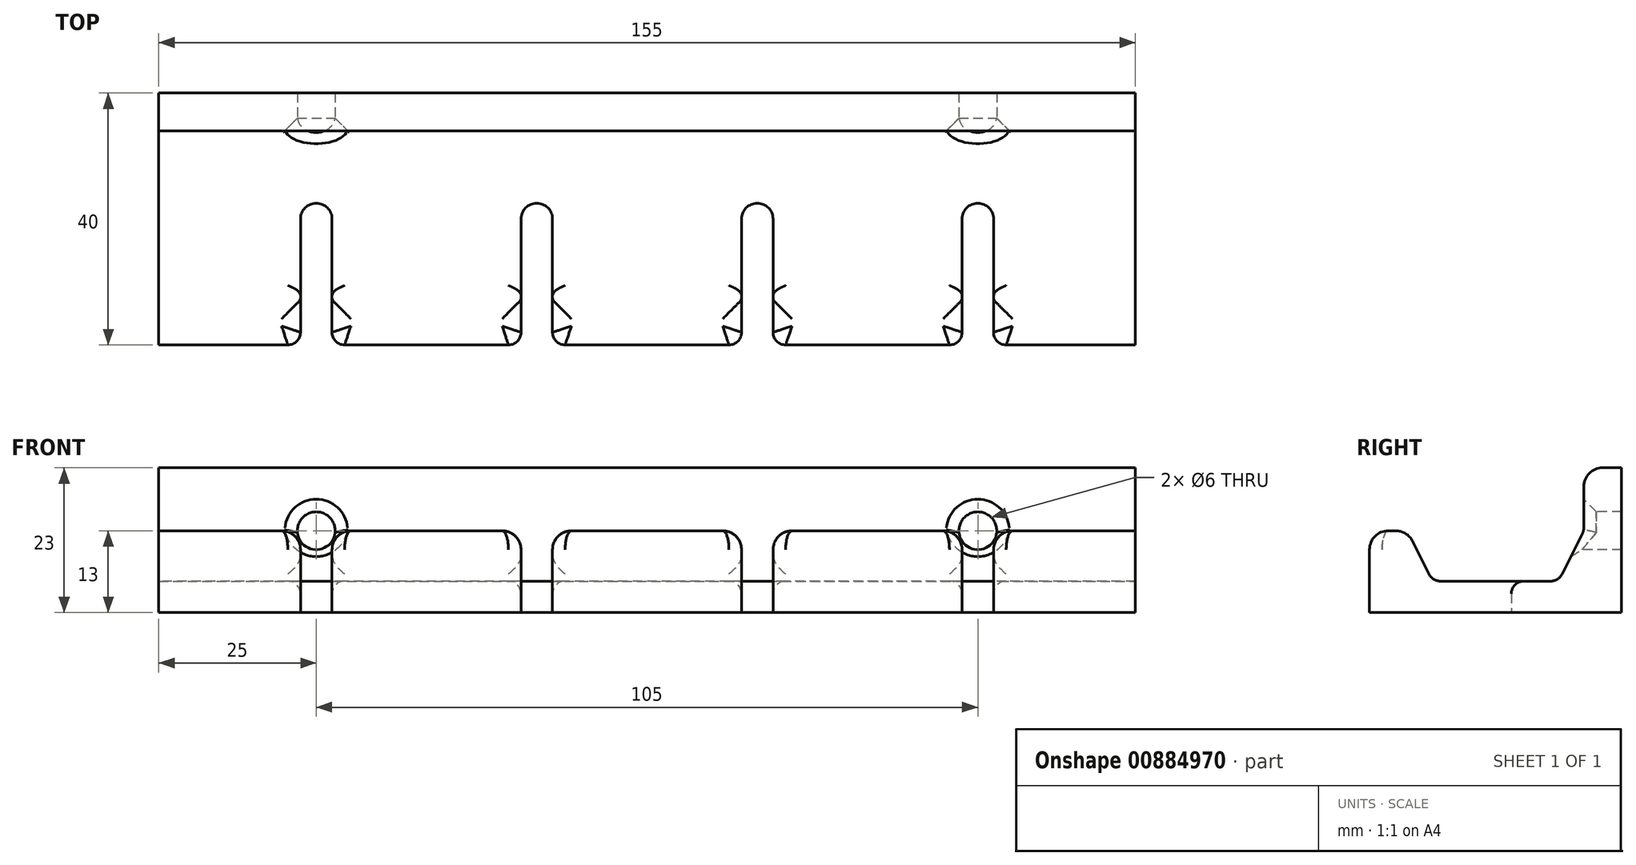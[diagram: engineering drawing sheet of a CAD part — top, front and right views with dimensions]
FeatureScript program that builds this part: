
annotation { "Feature Type Name" : "Feature", "Feature Type Description" : "" }
export const myFeature = defineFeature(function(context is Context, id is Id, definition is map)
    precondition{}
    {
        {
            var Q0;
            Q0=qCreatedBy(makeId("Top.planeOp"),FACE);
            var sketch = newSketch(context, id + "F0", { "sketchPlane" : qUnion([Q0])});
            skLineSegment(sketch, "E0.bottom", {"start": v(-77.5, 20) * mm, "end": v(77.5, 20) * mm});
            skLineSegment(sketch, "E0.top", {"start": v(-77.5, -20) * mm, "end": v(77.5, -20) * mm});
            skLineSegment(sketch, "E0.left", {"start": v(-77.5, 20) * mm, "end": v(-77.5, -20) * mm});
            skLineSegment(sketch, "E0.right", {"start": v(77.5, 20) * mm, "end": v(77.5, -20) * mm});
            skPoint(sketch, "E0.middle", {"position": v(0, 0) * mm});
            skSolve(sketch);
        }
        {
            var Q0;
            Q0=makeQuery(id+"F0.imprint","IMPRINT",FACE,{"disambiguationData":[TD([[makeQuery(id+"F0.imprint","IMPRINT",EDGE,{"derivedFrom":sQuery(id+"F0.wireOp",EDGE,"E0.bottom")}),-1.0]])]});
            extrude(context, id + "F1", {"entities" : qUnion([Q0]), "depth" : 5 * mm, "offsetDistance" : 25 * mm});
        }
        {
            var Q0;
            Q0=makeQuery(id+"F1.opExtrude","CAP_FACE",FACE,{"disambiguationData":[OSD([sQuery(id+"F0.wireOp",EDGE,"E0.bottom"),sQuery(id+"F0.wireOp",EDGE,"E0.top"),sQuery(id+"F0.wireOp",EDGE,"E0.left"),sQuery(id+"F0.wireOp",EDGE,"E0.right")])],"isStart":false});
            var sketch = newSketch(context, id + "F2", { "sketchPlane" : qUnion([Q0])});
            skLineSegment(sketch, "E1.bottom", {"start": v(-77.5, 10) * mm, "end": v(77.5, 10) * mm});
            skLineSegment(sketch, "E1.top", {"start": v(-77.5, -10) * mm, "end": v(77.5, -10) * mm});
            skLineSegment(sketch, "E1.left", {"start": v(-77.5, 10) * mm, "end": v(-77.5, -10) * mm});
            skLineSegment(sketch, "E1.right", {"start": v(77.5, 10) * mm, "end": v(77.5, -10) * mm});
            skPoint(sketch, "E1.middle", {"position": v(0, 0) * mm});
            skLineSegment(sketch, "E2.bottom", {"start": v(-77.5, 20) * mm, "end": v(77.5, 20) * mm});
            skLineSegment(sketch, "E2.top", {"start": v(-77.5, -20) * mm, "end": v(77.5, -20) * mm});
            skLineSegment(sketch, "E2.left", {"start": v(-77.5, 20) * mm, "end": v(-77.5, -20) * mm});
            skLineSegment(sketch, "E2.right", {"start": v(77.5, 20) * mm, "end": v(77.5, -20) * mm});
            skSolve(sketch);
        }
        {
            var Q0;
            {var subQ0=sQuery(id+"F2.wireOp",EDGE,"E1.bottom");Q0=makeQuery(id+"F2.imprint","IMPRINT",FACE,{"disambiguationData":[TD([[makeQuery(id+"F2.imprint","IMPRINT",EDGE,{"derivedFrom":subQ0}),1.0]])]});}
            var Q1;
            {var subQ0=sQuery(id+"F2.wireOp",EDGE,"E1.top");Q1=makeQuery(id+"F2.imprint","IMPRINT",FACE,{"disambiguationData":[TD([[makeQuery(id+"F2.imprint","IMPRINT",EDGE,{"derivedFrom":subQ0}),-1.0]])]});}
            extrude(context, id + "F3", {"entities" : qUnion([Q0, Q1]), "operationType" : NewBodyOperationType.ADD, "depth" : 8 * mm, "offsetDistance" : 25 * mm});
        }
        {
            var Q0;
            Q0=makeQuery(id+"F3.opExtrude","CAP_EDGE",EDGE,{"disambiguationData":[OSD([sQuery(id+"F2.wireOp",EDGE,"E1.bottom")])],"isStart":false});
            chamfer(context, id + "F4", {"entities" : qUnion([Q0]), "chamferType" : ChamferType.TWO_OFFSETS, "width1" : 8 * mm, "oppositeDirection" : true, "width2" : 4 * mm});
        }
        {
            var Q0;
            Q0=makeQuery(id+"F3.opExtrude","CAP_EDGE",EDGE,{"disambiguationData":[OSD([sQuery(id+"F2.wireOp",EDGE,"E1.top")])],"isStart":false});
            chamfer(context, id + "F5", {"entities" : qUnion([Q0]), "chamferType" : ChamferType.TWO_OFFSETS, "width1" : 8 * mm, "oppositeDirection" : false, "width2" : 4 * mm, "tangentPropagation" : true});
        }
        {
            var Q0;
            Q0=makeQuery(id+"F0.imprint","IMPRINT",FACE,{"disambiguationData":[TD([[makeQuery(id+"F0.imprint","IMPRINT",EDGE,{"derivedFrom":sQuery(id+"F0.wireOp",EDGE,"E0.bottom")}),-1.0]])]});
            var sketch = newSketch(context, id + "F6", { "sketchPlane" : qUnion([Q0])});
            skCircle(sketch, "E3", {"center": v(-52.5, 0) * mm, "radius": 2.5 * mm});
            skCircle(sketch, "E4.1.0.0", {"center": v(-17.5, 0) * mm, "radius": 2.5 * mm});
            skCircle(sketch, "E4.2.0.0", {"center": v(17.5, 0) * mm, "radius": 2.5 * mm});
            skCircle(sketch, "E4.3.0.0", {"center": v(52.5, 0) * mm, "radius": 2.5 * mm});
            skLineSegment(sketch, "E4.direction1", {"start": v(-52.5, 0) * mm, "end": v(-17.5, 0) * mm, "construction": true});
            skLineSegment(sketch, "E5", {"start": v(-50, 0) * mm, "end": v(-50, -25) * mm});
            skLineSegment(sketch, "E6", {"start": v(-55, 0) * mm, "end": v(-55, -25) * mm});
            skLineSegment(sketch, "E7", {"start": v(-20, 0) * mm, "end": v(-20, -25) * mm});
            skLineSegment(sketch, "E8", {"start": v(-80.14, 0) * mm, "end": v(82.26, 0) * mm, "construction": true});
            skLineSegment(sketch, "E9", {"start": v(-15, 0) * mm, "end": v(-15, -25) * mm});
            skLineSegment(sketch, "E10", {"start": v(15, 0) * mm, "end": v(15, -25) * mm});
            skLineSegment(sketch, "E11", {"start": v(20, 0) * mm, "end": v(20, -25) * mm});
            skLineSegment(sketch, "E12", {"start": v(50, 0) * mm, "end": v(50, -25) * mm});
            skLineSegment(sketch, "E13", {"start": v(55, 0) * mm, "end": v(55, -25) * mm});
            skLineSegment(sketch, "E14", {"start": v(-50, -25) * mm, "end": v(-55, -25) * mm});
            skLineSegment(sketch, "E15", {"start": v(-20, -25) * mm, "end": v(-15, -25) * mm});
            skLineSegment(sketch, "E16", {"start": v(15, -25) * mm, "end": v(20, -25) * mm});
            skLineSegment(sketch, "E17", {"start": v(50, -25) * mm, "end": v(55, -25) * mm});
            skSolve(sketch);
        }
        {
            var Q0;
            Q0=qSketchRegion(id+"F6",true);
            extrude(context, id + "F7", {"entities" : qUnion([Q0]), "operationType" : NewBodyOperationType.REMOVE, "depth" : 25 * mm, "offsetDistance" : 25 * mm});
        }
        {
            var Q0;
            Q0=makeQuery(id+"F3.opExtrude","CAP_FACE",FACE,{"disambiguationData":[OSD([sQuery(id+"F2.wireOp",EDGE,"E1.bottom"),sQuery(id+"F2.wireOp",EDGE,"E2.bottom"),sQuery(id+"F2.wireOp",EDGE,"E2.left"),sQuery(id+"F2.wireOp",EDGE,"E2.right")])],"isStart":false});
            extrude(context, id + "F8", {"entities" : qUnion([Q0]), "operationType" : NewBodyOperationType.ADD, "depth" : 10 * mm, "offsetDistance" : 25 * mm});
        }
        {
            var Q0;
            Q0=makeQuery(id+"F8.opExtrude","SWEPT_FACE",FACE,{"disambiguationData":[OSD([sQuery(id+"F2.wireOp",EDGE,"E1.bottom"),sQuery(id+"F2.wireOp",EDGE,"E2.bottom"),sQuery(id+"F2.wireOp",EDGE,"E2.left"),sQuery(id+"F2.wireOp",EDGE,"E2.right")])]});
            var sketch = newSketch(context, id + "F9", { "sketchPlane" : qUnion([Q0])});
            skCircle(sketch, "E18", {"center": v(-52.5, 13) * mm, "radius": 3 * mm});
            skCircle(sketch, "E19", {"center": v(52.5, 13) * mm, "radius": 3 * mm});
            skSolve(sketch);
        }
        {
            var Q0;
            Q0=qSketchRegion(id+"F9",true);
            extrude(context, id + "F10", {"entities" : qUnion([Q0]), "operationType" : NewBodyOperationType.REMOVE, "oppositeDirection" : true, "depth" : 15 * mm, "offsetDistance" : 25 * mm, "hasSecondDirection" : true, "secondDirectionOppositeDirection" : false, "secondDirectionDepth" : 15 * mm});
        }
        {
            var Q0;
            Q0=makeQuery(id+"F10.boolean.opBoolean","INTERSECT",EDGE,{"derivedFrom":[makeQuery(id+"F4.opChamfer","BLEND_FACE",FACE,{"disambiguationData":[OSD([sQuery(id+"F2.wireOp",EDGE,"E1.bottom")])]}),makeQuery(id+"F10.opExtrude","SWEPT_FACE",FACE,{"disambiguationData":[OSD([sQuery(id+"F9.wireOp",EDGE,"E18")])]})]});
            var Q1;
            Q1=makeQuery(id+"F10.boolean.opBoolean","INTERSECT",EDGE,{"derivedFrom":[makeQuery(id+"F8.opExtrude","SWEPT_FACE",FACE,{"disambiguationData":[OSD([sQuery(id+"F2.wireOp",EDGE,"E1.bottom"),sQuery(id+"F2.wireOp",EDGE,"E2.bottom"),sQuery(id+"F2.wireOp",EDGE,"E2.left"),sQuery(id+"F2.wireOp",EDGE,"E2.right")])]}),makeQuery(id+"F10.opExtrude","SWEPT_FACE",FACE,{"disambiguationData":[OSD([sQuery(id+"F9.wireOp",EDGE,"E18")])]})]});
            var Q2;
            Q2=makeQuery(id+"F10.boolean.opBoolean","INTERSECT",EDGE,{"derivedFrom":[makeQuery(id+"F4.opChamfer","BLEND_FACE",FACE,{"disambiguationData":[OSD([sQuery(id+"F2.wireOp",EDGE,"E1.bottom")])]}),makeQuery(id+"F10.opExtrude","SWEPT_FACE",FACE,{"disambiguationData":[OSD([sQuery(id+"F9.wireOp",EDGE,"E19")])]})]});
            var Q3;
            Q3=makeQuery(id+"F10.boolean.opBoolean","INTERSECT",EDGE,{"derivedFrom":[makeQuery(id+"F8.opExtrude","SWEPT_FACE",FACE,{"disambiguationData":[OSD([sQuery(id+"F2.wireOp",EDGE,"E1.bottom"),sQuery(id+"F2.wireOp",EDGE,"E2.bottom"),sQuery(id+"F2.wireOp",EDGE,"E2.left"),sQuery(id+"F2.wireOp",EDGE,"E2.right")])]}),makeQuery(id+"F10.opExtrude","SWEPT_FACE",FACE,{"disambiguationData":[OSD([sQuery(id+"F9.wireOp",EDGE,"E19")])]})]});
            chamfer(context, id + "F11", {"entities" : qUnion([Q0, Q1, Q2, Q3]), "width" : 2 * mm, "tangentPropagation" : true});
        }
        {
            var Q0;
            Q0=makeQuery(id+"F7.boolean.opBoolean","INTERSECT",EDGE,{"derivedFrom":[makeQuery(id+"F1.opExtrude","CAP_FACE",FACE,{"disambiguationData":[OSD([sQuery(id+"F0.wireOp",EDGE,"E0.bottom"),sQuery(id+"F0.wireOp",EDGE,"E0.top"),sQuery(id+"F0.wireOp",EDGE,"E0.left"),sQuery(id+"F0.wireOp",EDGE,"E0.right")])],"isStart":false}),makeQuery(id+"F7.opExtrude","SWEPT_FACE",FACE,{"disambiguationData":[OSD([sQuery(id+"F6.wireOp",EDGE,"E6")])]})]});
            var Q1;
            Q1=makeQuery(id+"F7.boolean.opBoolean","INTERSECT",EDGE,{"derivedFrom":[makeQuery(id+"F1.opExtrude","CAP_FACE",FACE,{"disambiguationData":[OSD([sQuery(id+"F0.wireOp",EDGE,"E0.bottom"),sQuery(id+"F0.wireOp",EDGE,"E0.top"),sQuery(id+"F0.wireOp",EDGE,"E0.left"),sQuery(id+"F0.wireOp",EDGE,"E0.right")])],"isStart":false}),makeQuery(id+"F7.opExtrude","SWEPT_FACE",FACE,{"disambiguationData":[OSD([sQuery(id+"F6.wireOp",EDGE,"E3")])]})]});
            var Q2;
            Q2=makeQuery(id+"F7.boolean.opBoolean","INTERSECT",EDGE,{"derivedFrom":[makeQuery(id+"F1.opExtrude","CAP_FACE",FACE,{"disambiguationData":[OSD([sQuery(id+"F0.wireOp",EDGE,"E0.bottom"),sQuery(id+"F0.wireOp",EDGE,"E0.top"),sQuery(id+"F0.wireOp",EDGE,"E0.left"),sQuery(id+"F0.wireOp",EDGE,"E0.right")])],"isStart":false}),makeQuery(id+"F7.opExtrude","SWEPT_FACE",FACE,{"disambiguationData":[OSD([sQuery(id+"F6.wireOp",EDGE,"E5")])]})]});
            var Q3;
            Q3=makeQuery(id+"F7.boolean.opBoolean","INTERSECT",EDGE,{"derivedFrom":[makeQuery(id+"F1.opExtrude","CAP_FACE",FACE,{"disambiguationData":[OSD([sQuery(id+"F0.wireOp",EDGE,"E0.bottom"),sQuery(id+"F0.wireOp",EDGE,"E0.top"),sQuery(id+"F0.wireOp",EDGE,"E0.left"),sQuery(id+"F0.wireOp",EDGE,"E0.right")])],"isStart":false}),makeQuery(id+"F7.opExtrude","SWEPT_FACE",FACE,{"disambiguationData":[OSD([sQuery(id+"F6.wireOp",EDGE,"E7")])]})]});
            var Q4;
            Q4=makeQuery(id+"F7.boolean.opBoolean","INTERSECT",EDGE,{"derivedFrom":[makeQuery(id+"F1.opExtrude","CAP_FACE",FACE,{"disambiguationData":[OSD([sQuery(id+"F0.wireOp",EDGE,"E0.bottom"),sQuery(id+"F0.wireOp",EDGE,"E0.top"),sQuery(id+"F0.wireOp",EDGE,"E0.left"),sQuery(id+"F0.wireOp",EDGE,"E0.right")])],"isStart":false}),makeQuery(id+"F7.opExtrude","SWEPT_FACE",FACE,{"disambiguationData":[OSD([sQuery(id+"F6.wireOp",EDGE,"E4.1.0.0")])]})]});
            var Q5;
            Q5=makeQuery(id+"F7.boolean.opBoolean","INTERSECT",EDGE,{"derivedFrom":[makeQuery(id+"F1.opExtrude","CAP_FACE",FACE,{"disambiguationData":[OSD([sQuery(id+"F0.wireOp",EDGE,"E0.bottom"),sQuery(id+"F0.wireOp",EDGE,"E0.top"),sQuery(id+"F0.wireOp",EDGE,"E0.left"),sQuery(id+"F0.wireOp",EDGE,"E0.right")])],"isStart":false}),makeQuery(id+"F7.opExtrude","SWEPT_FACE",FACE,{"disambiguationData":[OSD([sQuery(id+"F6.wireOp",EDGE,"E9")])]})]});
            var Q6;
            Q6=makeQuery(id+"F7.boolean.opBoolean","INTERSECT",EDGE,{"derivedFrom":[makeQuery(id+"F1.opExtrude","CAP_FACE",FACE,{"disambiguationData":[OSD([sQuery(id+"F0.wireOp",EDGE,"E0.bottom"),sQuery(id+"F0.wireOp",EDGE,"E0.top"),sQuery(id+"F0.wireOp",EDGE,"E0.left"),sQuery(id+"F0.wireOp",EDGE,"E0.right")])],"isStart":false}),makeQuery(id+"F7.opExtrude","SWEPT_FACE",FACE,{"disambiguationData":[OSD([sQuery(id+"F6.wireOp",EDGE,"E10")])]})]});
            var Q7;
            Q7=makeQuery(id+"F7.boolean.opBoolean","INTERSECT",EDGE,{"derivedFrom":[makeQuery(id+"F1.opExtrude","CAP_FACE",FACE,{"disambiguationData":[OSD([sQuery(id+"F0.wireOp",EDGE,"E0.bottom"),sQuery(id+"F0.wireOp",EDGE,"E0.top"),sQuery(id+"F0.wireOp",EDGE,"E0.left"),sQuery(id+"F0.wireOp",EDGE,"E0.right")])],"isStart":false}),makeQuery(id+"F7.opExtrude","SWEPT_FACE",FACE,{"disambiguationData":[OSD([sQuery(id+"F6.wireOp",EDGE,"E12")])]})]});
            var Q8;
            Q8=makeQuery(id+"F7.boolean.opBoolean","COPY",EDGE,{"derivedFrom":makeQuery(id+"F7.opExtrude","CAP_EDGE",EDGE,{"disambiguationData":[OSD([sQuery(id+"F6.wireOp",EDGE,"E5")])],"isStart":true})});
            var Q9;
            Q9=makeQuery(id+"F7.boolean.opBoolean","COPY",EDGE,{"derivedFrom":makeQuery(id+"F7.opExtrude","CAP_EDGE",EDGE,{"disambiguationData":[OSD([sQuery(id+"F6.wireOp",EDGE,"E9")])],"isStart":true})});
            var Q10;
            Q10=makeQuery(id+"F7.boolean.opBoolean","COPY",EDGE,{"derivedFrom":makeQuery(id+"F7.opExtrude","CAP_EDGE",EDGE,{"disambiguationData":[OSD([sQuery(id+"F6.wireOp",EDGE,"E11")])],"isStart":true})});
            var Q11;
            Q11=makeQuery(id+"F7.boolean.opBoolean","COPY",EDGE,{"derivedFrom":makeQuery(id+"F7.opExtrude","CAP_EDGE",EDGE,{"disambiguationData":[OSD([sQuery(id+"F6.wireOp",EDGE,"E13")])],"isStart":true})});
            var Q12;
            Q12=makeQuery(id+"F7.boolean.opBoolean","INTERSECT",EDGE,{"derivedFrom":[makeQuery(id+"F3.boolean.opBoolean","MERGE",FACE,{"derivedFrom":[makeQuery(id+"F1.opExtrude","SWEPT_FACE",FACE,{"disambiguationData":[OSD([sQuery(id+"F0.wireOp",EDGE,"E0.top")])]}),makeQuery(id+"F3.opExtrude","SWEPT_FACE",FACE,{"disambiguationData":[OSD([sQuery(id+"F2.wireOp",EDGE,"E2.top")])]})]}),makeQuery(id+"F7.opExtrude","SWEPT_FACE",FACE,{"disambiguationData":[OSD([sQuery(id+"F6.wireOp",EDGE,"E6")])]})]});
            var Q13;
            Q13=makeQuery(id+"F7.boolean.opBoolean","INTERSECT",EDGE,{"derivedFrom":[makeQuery(id+"F3.boolean.opBoolean","MERGE",FACE,{"derivedFrom":[makeQuery(id+"F1.opExtrude","SWEPT_FACE",FACE,{"disambiguationData":[OSD([sQuery(id+"F0.wireOp",EDGE,"E0.top")])]}),makeQuery(id+"F3.opExtrude","SWEPT_FACE",FACE,{"disambiguationData":[OSD([sQuery(id+"F2.wireOp",EDGE,"E2.top")])]})]}),makeQuery(id+"F7.opExtrude","SWEPT_FACE",FACE,{"disambiguationData":[OSD([sQuery(id+"F6.wireOp",EDGE,"E5")])]})]});
            var Q14;
            Q14=makeQuery(id+"F7.boolean.opBoolean","INTERSECT",EDGE,{"derivedFrom":[makeQuery(id+"F3.boolean.opBoolean","MERGE",FACE,{"derivedFrom":[makeQuery(id+"F1.opExtrude","SWEPT_FACE",FACE,{"disambiguationData":[OSD([sQuery(id+"F0.wireOp",EDGE,"E0.top")])]}),makeQuery(id+"F3.opExtrude","SWEPT_FACE",FACE,{"disambiguationData":[OSD([sQuery(id+"F2.wireOp",EDGE,"E2.top")])]})]}),makeQuery(id+"F7.opExtrude","SWEPT_FACE",FACE,{"disambiguationData":[OSD([sQuery(id+"F6.wireOp",EDGE,"E7")])]})]});
            var Q15;
            Q15=makeQuery(id+"F7.boolean.opBoolean","INTERSECT",EDGE,{"derivedFrom":[makeQuery(id+"F3.boolean.opBoolean","MERGE",FACE,{"derivedFrom":[makeQuery(id+"F1.opExtrude","SWEPT_FACE",FACE,{"disambiguationData":[OSD([sQuery(id+"F0.wireOp",EDGE,"E0.top")])]}),makeQuery(id+"F3.opExtrude","SWEPT_FACE",FACE,{"disambiguationData":[OSD([sQuery(id+"F2.wireOp",EDGE,"E2.top")])]})]}),makeQuery(id+"F7.opExtrude","SWEPT_FACE",FACE,{"disambiguationData":[OSD([sQuery(id+"F6.wireOp",EDGE,"E9")])]})]});
            var Q16;
            Q16=makeQuery(id+"F7.boolean.opBoolean","INTERSECT",EDGE,{"derivedFrom":[makeQuery(id+"F3.boolean.opBoolean","MERGE",FACE,{"derivedFrom":[makeQuery(id+"F1.opExtrude","SWEPT_FACE",FACE,{"disambiguationData":[OSD([sQuery(id+"F0.wireOp",EDGE,"E0.top")])]}),makeQuery(id+"F3.opExtrude","SWEPT_FACE",FACE,{"disambiguationData":[OSD([sQuery(id+"F2.wireOp",EDGE,"E2.top")])]})]}),makeQuery(id+"F7.opExtrude","SWEPT_FACE",FACE,{"disambiguationData":[OSD([sQuery(id+"F6.wireOp",EDGE,"E10")])]})]});
            var Q17;
            Q17=makeQuery(id+"F7.boolean.opBoolean","INTERSECT",EDGE,{"derivedFrom":[makeQuery(id+"F3.boolean.opBoolean","MERGE",FACE,{"derivedFrom":[makeQuery(id+"F1.opExtrude","SWEPT_FACE",FACE,{"disambiguationData":[OSD([sQuery(id+"F0.wireOp",EDGE,"E0.top")])]}),makeQuery(id+"F3.opExtrude","SWEPT_FACE",FACE,{"disambiguationData":[OSD([sQuery(id+"F2.wireOp",EDGE,"E2.top")])]})]}),makeQuery(id+"F7.opExtrude","SWEPT_FACE",FACE,{"disambiguationData":[OSD([sQuery(id+"F6.wireOp",EDGE,"E11")])]})]});
            var Q18;
            Q18=makeQuery(id+"F7.boolean.opBoolean","INTERSECT",EDGE,{"derivedFrom":[makeQuery(id+"F3.boolean.opBoolean","MERGE",FACE,{"derivedFrom":[makeQuery(id+"F1.opExtrude","SWEPT_FACE",FACE,{"disambiguationData":[OSD([sQuery(id+"F0.wireOp",EDGE,"E0.top")])]}),makeQuery(id+"F3.opExtrude","SWEPT_FACE",FACE,{"disambiguationData":[OSD([sQuery(id+"F2.wireOp",EDGE,"E2.top")])]})]}),makeQuery(id+"F7.opExtrude","SWEPT_FACE",FACE,{"disambiguationData":[OSD([sQuery(id+"F6.wireOp",EDGE,"E12")])]})]});
            var Q19;
            Q19=makeQuery(id+"F7.boolean.opBoolean","INTERSECT",EDGE,{"derivedFrom":[makeQuery(id+"F3.boolean.opBoolean","MERGE",FACE,{"derivedFrom":[makeQuery(id+"F1.opExtrude","SWEPT_FACE",FACE,{"disambiguationData":[OSD([sQuery(id+"F0.wireOp",EDGE,"E0.top")])]}),makeQuery(id+"F3.opExtrude","SWEPT_FACE",FACE,{"disambiguationData":[OSD([sQuery(id+"F2.wireOp",EDGE,"E2.top")])]})]}),makeQuery(id+"F7.opExtrude","SWEPT_FACE",FACE,{"disambiguationData":[OSD([sQuery(id+"F6.wireOp",EDGE,"E13")])]})]});
            var Q20;
            {var subQ0=makeQuery(id+"F1.opExtrude","CAP_FACE",FACE,{"disambiguationData":[OSD([sQuery(id+"F0.wireOp",EDGE,"E0.bottom"),sQuery(id+"F0.wireOp",EDGE,"E0.top"),sQuery(id+"F0.wireOp",EDGE,"E0.left"),sQuery(id+"F0.wireOp",EDGE,"E0.right")])],"isStart":false});var subQ1=sQuery(id+"F2.wireOp",EDGE,"E1.top");Q20=makeQuery(id+"F7.boolean.opBoolean","SPLIT",EDGE,{"disambiguationData":[TD([makeQuery(id+"F7.opExtrude","SWEPT_FACE",FACE,{"disambiguationData":[OSD([sQuery(id+"F6.wireOp",EDGE,"E9")])]})])],"derivedFrom":makeQuery(id+"F5.opChamfer","BLEND_EDGE",EDGE,{"blendedFrom":[makeQuery(id+"F3.opExtrude","CAP_EDGE",EDGE,{"disambiguationData":[OSD([subQ1])],"isStart":false}),subQ0],"blendedInto":[subQ0]})});}
            var Q21;
            {var subQ0=makeQuery(id+"F1.opExtrude","CAP_FACE",FACE,{"disambiguationData":[OSD([sQuery(id+"F0.wireOp",EDGE,"E0.bottom"),sQuery(id+"F0.wireOp",EDGE,"E0.top"),sQuery(id+"F0.wireOp",EDGE,"E0.left"),sQuery(id+"F0.wireOp",EDGE,"E0.right")])],"isStart":false});var subQ1=sQuery(id+"F2.wireOp",EDGE,"E1.top");Q21=makeQuery(id+"F7.boolean.opBoolean","SPLIT",EDGE,{"disambiguationData":[TD([makeQuery(id+"F7.opExtrude","SWEPT_FACE",FACE,{"disambiguationData":[OSD([sQuery(id+"F6.wireOp",EDGE,"E5")])]})])],"derivedFrom":makeQuery(id+"F5.opChamfer","BLEND_EDGE",EDGE,{"blendedFrom":[makeQuery(id+"F3.opExtrude","CAP_EDGE",EDGE,{"disambiguationData":[OSD([subQ1])],"isStart":false}),subQ0],"blendedInto":[subQ0]})});}
            var Q22;
            {var subQ1=sQuery(id+"F0.wireOp",EDGE,"E0.left");var subQ2=sQuery(id+"F2.wireOp",EDGE,"E1.top");var subQ3=makeQuery(id+"F1.opExtrude","CAP_FACE",FACE,{"disambiguationData":[OSD([sQuery(id+"F0.wireOp",EDGE,"E0.bottom"),sQuery(id+"F0.wireOp",EDGE,"E0.top"),subQ1,sQuery(id+"F0.wireOp",EDGE,"E0.right")])],"isStart":false});Q22=makeQuery(id+"F7.boolean.opBoolean","SPLIT",EDGE,{"disambiguationData":[TD([makeQuery(id+"F1.opExtrude","SWEPT_FACE",FACE,{"disambiguationData":[OSD([subQ1])]})])],"derivedFrom":makeQuery(id+"F5.opChamfer","BLEND_EDGE",EDGE,{"blendedFrom":[makeQuery(id+"F3.opExtrude","CAP_EDGE",EDGE,{"disambiguationData":[OSD([subQ2])],"isStart":false}),subQ3],"blendedInto":[subQ3]})});}
            var Q23;
            {var subQ0=makeQuery(id+"F1.opExtrude","CAP_FACE",FACE,{"disambiguationData":[OSD([sQuery(id+"F0.wireOp",EDGE,"E0.bottom"),sQuery(id+"F0.wireOp",EDGE,"E0.top"),sQuery(id+"F0.wireOp",EDGE,"E0.left"),sQuery(id+"F0.wireOp",EDGE,"E0.right")])],"isStart":false});var subQ1=sQuery(id+"F2.wireOp",EDGE,"E1.top");Q23=makeQuery(id+"F7.boolean.opBoolean","SPLIT",EDGE,{"disambiguationData":[TD([makeQuery(id+"F7.opExtrude","SWEPT_FACE",FACE,{"disambiguationData":[OSD([sQuery(id+"F6.wireOp",EDGE,"E11")])]})])],"derivedFrom":makeQuery(id+"F5.opChamfer","BLEND_EDGE",EDGE,{"blendedFrom":[makeQuery(id+"F3.opExtrude","CAP_EDGE",EDGE,{"disambiguationData":[OSD([subQ1])],"isStart":false}),subQ0],"blendedInto":[subQ0]})});}
            var Q24;
            {var subQ1=sQuery(id+"F2.wireOp",EDGE,"E1.top");var subQ2=sQuery(id+"F0.wireOp",EDGE,"E0.right");var subQ3=makeQuery(id+"F1.opExtrude","CAP_FACE",FACE,{"disambiguationData":[OSD([sQuery(id+"F0.wireOp",EDGE,"E0.bottom"),sQuery(id+"F0.wireOp",EDGE,"E0.top"),sQuery(id+"F0.wireOp",EDGE,"E0.left"),subQ2])],"isStart":false});Q24=makeQuery(id+"F7.boolean.opBoolean","SPLIT",EDGE,{"disambiguationData":[TD([makeQuery(id+"F1.opExtrude","SWEPT_FACE",FACE,{"disambiguationData":[OSD([subQ2])]})])],"derivedFrom":makeQuery(id+"F5.opChamfer","BLEND_EDGE",EDGE,{"blendedFrom":[makeQuery(id+"F3.opExtrude","CAP_EDGE",EDGE,{"disambiguationData":[OSD([subQ1])],"isStart":false}),subQ3],"blendedInto":[subQ3]})});}
            var Q25;
            Q25=makeQuery(id+"F4.opChamfer","BLEND_EDGE",EDGE,{"blendedFrom":[makeQuery(id+"F3.opExtrude","CAP_EDGE",EDGE,{"disambiguationData":[OSD([sQuery(id+"F2.wireOp",EDGE,"E1.bottom")])],"isStart":false}),makeQuery(id+"F1.opExtrude","CAP_FACE",FACE,{"disambiguationData":[OSD([sQuery(id+"F0.wireOp",EDGE,"E0.bottom"),sQuery(id+"F0.wireOp",EDGE,"E0.top"),sQuery(id+"F0.wireOp",EDGE,"E0.left"),sQuery(id+"F0.wireOp",EDGE,"E0.right")])],"isStart":false})],"blendedInto":[makeQuery(id+"F1.opExtrude","CAP_FACE",FACE,{"disambiguationData":[OSD([sQuery(id+"F0.wireOp",EDGE,"E0.bottom"),sQuery(id+"F0.wireOp",EDGE,"E0.top"),sQuery(id+"F0.wireOp",EDGE,"E0.left"),sQuery(id+"F0.wireOp",EDGE,"E0.right")])],"isStart":false})]});
            var Q26;
            {var subQ0=sQuery(id+"F2.wireOp",EDGE,"E1.bottom");var subQ1=sQuery(id+"F2.wireOp",EDGE,"E2.left");var subQ2=sQuery(id+"F2.wireOp",EDGE,"E2.bottom");var subQ3=sQuery(id+"F2.wireOp",EDGE,"E2.right");Q26=makeQuery(id+"F10.boolean.opBoolean","SPLIT",EDGE,{"disambiguationData":[TD([makeQuery(id+"F1.opExtrude","SWEPT_FACE",FACE,{"disambiguationData":[OSD([sQuery(id+"F0.wireOp",EDGE,"E0.left")])]}),makeQuery(id+"F3.opExtrude","SWEPT_FACE",FACE,{"disambiguationData":[OSD([subQ1]),TDD([makeQuery(id+"F2.imprint","IMPRINT",EDGE,{"disambiguationData":[TD([[makeQuery(id+"F2.imprint","INTERSECT",VERTEX,{"derivedFrom":[subQ2,subQ1]}),-1.0]])],"derivedFrom":subQ1})])]}),makeQuery(id+"F3.opExtrude","SWEPT_FACE",FACE,{"disambiguationData":[OSD([subQ1]),TDD([makeQuery(id+"F2.imprint","IMPRINT",EDGE,{"disambiguationData":[TD([[makeQuery(id+"F2.imprint","INTERSECT",VERTEX,{"derivedFrom":[sQuery(id+"F2.wireOp",EDGE,"E2.top"),subQ1]}),1.0]])],"derivedFrom":subQ1})])]}),makeQuery(id+"F4.opChamfer","BLEND_FACE",FACE,{"disambiguationData":[OSD([subQ0])]}),makeQuery(id+"F8.opExtrude","SWEPT_FACE",FACE,{"disambiguationData":[OSD([subQ0,subQ2,subQ1,subQ3])]}),makeQuery(id+"F8.opExtrude","SWEPT_FACE",FACE,{"disambiguationData":[OSD([subQ1])]}),makeQuery(id+"F10.opExtrude","SWEPT_FACE",FACE,{"disambiguationData":[OSD([sQuery(id+"F9.wireOp",EDGE,"E18")])]})])],"derivedFrom":makeQuery(id+"F8.boolean.opBoolean","MERGE",EDGE,{"derivedFrom":[makeQuery(id+"F4.opChamfer","BLEND_EDGE",EDGE,{"blendedFrom":[makeQuery(id+"F3.opExtrude","CAP_EDGE",EDGE,{"disambiguationData":[OSD([subQ0])],"isStart":false}),makeQuery(id+"F3.opExtrude","CAP_FACE",FACE,{"disambiguationData":[OSD([subQ0,subQ2,subQ1,subQ3])],"isStart":false})],"blendedInto":[makeQuery(id+"F3.opExtrude","CAP_FACE",FACE,{"disambiguationData":[OSD([subQ0,subQ2,subQ1,subQ3])],"isStart":false})]}),makeQuery(id+"F8.opExtrude","CAP_EDGE",EDGE,{"disambiguationData":[OSD([subQ0,subQ2,subQ1,subQ3])],"isStart":true})]})});}
            var Q27;
            {var subQ0=sQuery(id+"F2.wireOp",EDGE,"E1.bottom");var subQ1=sQuery(id+"F2.wireOp",EDGE,"E2.right");var subQ2=sQuery(id+"F2.wireOp",EDGE,"E2.left");var subQ3=sQuery(id+"F2.wireOp",EDGE,"E2.bottom");Q27=makeQuery(id+"F10.boolean.opBoolean","SPLIT",EDGE,{"disambiguationData":[TD([makeQuery(id+"F4.opChamfer","BLEND_FACE",FACE,{"disambiguationData":[OSD([subQ0])]}),makeQuery(id+"F8.opExtrude","SWEPT_FACE",FACE,{"disambiguationData":[OSD([subQ0,subQ3,subQ2,subQ1])]}),makeQuery(id+"F10.opExtrude","SWEPT_FACE",FACE,{"disambiguationData":[OSD([sQuery(id+"F9.wireOp",EDGE,"E18")])]}),makeQuery(id+"F10.opExtrude","SWEPT_FACE",FACE,{"disambiguationData":[OSD([sQuery(id+"F9.wireOp",EDGE,"E19")])]})])],"derivedFrom":makeQuery(id+"F8.boolean.opBoolean","MERGE",EDGE,{"derivedFrom":[makeQuery(id+"F4.opChamfer","BLEND_EDGE",EDGE,{"blendedFrom":[makeQuery(id+"F3.opExtrude","CAP_EDGE",EDGE,{"disambiguationData":[OSD([subQ0])],"isStart":false}),makeQuery(id+"F3.opExtrude","CAP_FACE",FACE,{"disambiguationData":[OSD([subQ0,subQ3,subQ2,subQ1])],"isStart":false})],"blendedInto":[makeQuery(id+"F3.opExtrude","CAP_FACE",FACE,{"disambiguationData":[OSD([subQ0,subQ3,subQ2,subQ1])],"isStart":false})]}),makeQuery(id+"F8.opExtrude","CAP_EDGE",EDGE,{"disambiguationData":[OSD([subQ0,subQ3,subQ2,subQ1])],"isStart":true})]})});}
            var Q28;
            {var subQ0=sQuery(id+"F2.wireOp",EDGE,"E2.right");var subQ1=sQuery(id+"F2.wireOp",EDGE,"E2.bottom");var subQ2=sQuery(id+"F2.wireOp",EDGE,"E1.bottom");var subQ3=sQuery(id+"F2.wireOp",EDGE,"E2.left");Q28=makeQuery(id+"F10.boolean.opBoolean","SPLIT",EDGE,{"disambiguationData":[TD([makeQuery(id+"F1.opExtrude","SWEPT_FACE",FACE,{"disambiguationData":[OSD([sQuery(id+"F0.wireOp",EDGE,"E0.right")])]}),makeQuery(id+"F3.opExtrude","SWEPT_FACE",FACE,{"disambiguationData":[OSD([subQ0]),TDD([makeQuery(id+"F2.imprint","IMPRINT",EDGE,{"disambiguationData":[TD([[makeQuery(id+"F2.imprint","INTERSECT",VERTEX,{"derivedFrom":[subQ1,subQ0]}),-1.0]])],"derivedFrom":subQ0})])]}),makeQuery(id+"F3.opExtrude","SWEPT_FACE",FACE,{"disambiguationData":[OSD([subQ0]),TDD([makeQuery(id+"F2.imprint","IMPRINT",EDGE,{"disambiguationData":[TD([[makeQuery(id+"F2.imprint","INTERSECT",VERTEX,{"derivedFrom":[sQuery(id+"F2.wireOp",EDGE,"E2.top"),subQ0]}),1.0]])],"derivedFrom":subQ0})])]}),makeQuery(id+"F4.opChamfer","BLEND_FACE",FACE,{"disambiguationData":[OSD([subQ2])]}),makeQuery(id+"F8.opExtrude","SWEPT_FACE",FACE,{"disambiguationData":[OSD([subQ2,subQ1,subQ3,subQ0])]}),makeQuery(id+"F8.opExtrude","SWEPT_FACE",FACE,{"disambiguationData":[OSD([subQ0])]}),makeQuery(id+"F10.opExtrude","SWEPT_FACE",FACE,{"disambiguationData":[OSD([sQuery(id+"F9.wireOp",EDGE,"E19")])]})])],"derivedFrom":makeQuery(id+"F8.boolean.opBoolean","MERGE",EDGE,{"derivedFrom":[makeQuery(id+"F4.opChamfer","BLEND_EDGE",EDGE,{"blendedFrom":[makeQuery(id+"F3.opExtrude","CAP_EDGE",EDGE,{"disambiguationData":[OSD([subQ2])],"isStart":false}),makeQuery(id+"F3.opExtrude","CAP_FACE",FACE,{"disambiguationData":[OSD([subQ2,subQ1,subQ3,subQ0])],"isStart":false})],"blendedInto":[makeQuery(id+"F3.opExtrude","CAP_FACE",FACE,{"disambiguationData":[OSD([subQ2,subQ1,subQ3,subQ0])],"isStart":false})]}),makeQuery(id+"F8.opExtrude","CAP_EDGE",EDGE,{"disambiguationData":[OSD([subQ2,subQ1,subQ3,subQ0])],"isStart":true})]})});}
            fillet(context, id + "F12", {"entities" : qUnion([Q0, Q1, Q2, Q3, Q4, Q5, Q6, Q7, Q8, Q9, Q10, Q11, Q12, Q13, Q14, Q15, Q16, Q17, Q18, Q19, Q20, Q21, Q22, Q23, Q24, Q25, Q26, Q27, Q28]), "radius" : 2 * mm, "tangentPropagation" : true, "allowEdgeOverflow" : false});
        }
        {
            var Q0;
            Q0=makeQuery(id+"F8.opExtrude","CAP_EDGE",EDGE,{"disambiguationData":[OSD([sQuery(id+"F2.wireOp",EDGE,"E1.bottom"),sQuery(id+"F2.wireOp",EDGE,"E2.bottom"),sQuery(id+"F2.wireOp",EDGE,"E2.left"),sQuery(id+"F2.wireOp",EDGE,"E2.right")])],"isStart":false});
            var Q1;
            {var subQ0=sQuery(id+"F2.wireOp",EDGE,"E2.left");var subQ1=sQuery(id+"F2.wireOp",EDGE,"E2.top");var subQ2=sQuery(id+"F2.wireOp",EDGE,"E1.top");var subQ3=makeQuery(id+"F3.opExtrude","CAP_FACE",FACE,{"disambiguationData":[OSD([subQ2,subQ1,subQ0,sQuery(id+"F2.wireOp",EDGE,"E2.right")])],"isStart":false});Q1=makeQuery(id+"F7.boolean.opBoolean","SPLIT",EDGE,{"disambiguationData":[TD([makeQuery(id+"F1.opExtrude","SWEPT_FACE",FACE,{"disambiguationData":[OSD([sQuery(id+"F0.wireOp",EDGE,"E0.left")])]})])],"derivedFrom":makeQuery(id+"F5.opChamfer","BLEND_EDGE",EDGE,{"blendedFrom":[makeQuery(id+"F3.opExtrude","CAP_EDGE",EDGE,{"disambiguationData":[OSD([subQ2])],"isStart":false}),subQ3],"blendedInto":[subQ3]})});}
            var Q2;
            {var subQ0=sQuery(id+"F2.wireOp",EDGE,"E2.top");Q2=makeQuery(id+"F7.boolean.opBoolean","SPLIT",EDGE,{"disambiguationData":[TD([makeQuery(id+"F1.opExtrude","SWEPT_FACE",FACE,{"disambiguationData":[OSD([sQuery(id+"F0.wireOp",EDGE,"E0.left")])]})])],"derivedFrom":makeQuery(id+"F3.opExtrude","CAP_EDGE",EDGE,{"disambiguationData":[OSD([subQ0])],"isStart":false})});}
            var Q3;
            {var subQ0=sQuery(id+"F2.wireOp",EDGE,"E2.top");var subQ1=sQuery(id+"F2.wireOp",EDGE,"E1.top");Q3=makeQuery(id+"F7.boolean.opBoolean","SPLIT",FACE,{"disambiguationData":[TD([makeQuery(id+"F7.opExtrude","SWEPT_FACE",FACE,{"disambiguationData":[OSD([sQuery(id+"F6.wireOp",EDGE,"E5")])]})])],"derivedFrom":makeQuery(id+"F3.opExtrude","CAP_FACE",FACE,{"disambiguationData":[OSD([subQ1,subQ0,sQuery(id+"F2.wireOp",EDGE,"E2.left"),sQuery(id+"F2.wireOp",EDGE,"E2.right")])],"isStart":false})});}
            var Q4;
            {var subQ0=sQuery(id+"F2.wireOp",EDGE,"E1.top");var subQ1=sQuery(id+"F2.wireOp",EDGE,"E2.top");Q4=makeQuery(id+"F7.boolean.opBoolean","SPLIT",FACE,{"disambiguationData":[TD([makeQuery(id+"F7.opExtrude","SWEPT_FACE",FACE,{"disambiguationData":[OSD([sQuery(id+"F6.wireOp",EDGE,"E9")])]})])],"derivedFrom":makeQuery(id+"F3.opExtrude","CAP_FACE",FACE,{"disambiguationData":[OSD([subQ0,subQ1,sQuery(id+"F2.wireOp",EDGE,"E2.left"),sQuery(id+"F2.wireOp",EDGE,"E2.right")])],"isStart":false})});}
            var Q5;
            {var subQ0=sQuery(id+"F2.wireOp",EDGE,"E1.top");var subQ1=sQuery(id+"F2.wireOp",EDGE,"E2.top");Q5=makeQuery(id+"F7.boolean.opBoolean","SPLIT",FACE,{"disambiguationData":[TD([makeQuery(id+"F7.opExtrude","SWEPT_FACE",FACE,{"disambiguationData":[OSD([sQuery(id+"F6.wireOp",EDGE,"E11")])]})])],"derivedFrom":makeQuery(id+"F3.opExtrude","CAP_FACE",FACE,{"disambiguationData":[OSD([subQ0,subQ1,sQuery(id+"F2.wireOp",EDGE,"E2.left"),sQuery(id+"F2.wireOp",EDGE,"E2.right")])],"isStart":false})});}
            var Q6;
            {var subQ0=sQuery(id+"F2.wireOp",EDGE,"E2.right");var subQ1=sQuery(id+"F2.wireOp",EDGE,"E2.top");var subQ2=sQuery(id+"F2.wireOp",EDGE,"E1.top");var subQ3=makeQuery(id+"F3.opExtrude","CAP_FACE",FACE,{"disambiguationData":[OSD([subQ2,subQ1,sQuery(id+"F2.wireOp",EDGE,"E2.left"),subQ0])],"isStart":false});Q6=makeQuery(id+"F7.boolean.opBoolean","SPLIT",EDGE,{"disambiguationData":[TD([makeQuery(id+"F1.opExtrude","SWEPT_FACE",FACE,{"disambiguationData":[OSD([sQuery(id+"F0.wireOp",EDGE,"E0.right")])]})])],"derivedFrom":makeQuery(id+"F5.opChamfer","BLEND_EDGE",EDGE,{"blendedFrom":[makeQuery(id+"F3.opExtrude","CAP_EDGE",EDGE,{"disambiguationData":[OSD([subQ2])],"isStart":false}),subQ3],"blendedInto":[subQ3]})});}
            var Q7;
            {var subQ0=sQuery(id+"F2.wireOp",EDGE,"E2.top");Q7=makeQuery(id+"F7.boolean.opBoolean","SPLIT",EDGE,{"disambiguationData":[TD([makeQuery(id+"F1.opExtrude","SWEPT_FACE",FACE,{"disambiguationData":[OSD([sQuery(id+"F0.wireOp",EDGE,"E0.right")])]})])],"derivedFrom":makeQuery(id+"F3.opExtrude","CAP_EDGE",EDGE,{"disambiguationData":[OSD([subQ0])],"isStart":false})});}
            fillet(context, id + "F13", {"entities" : qUnion([Q0, Q1, Q2, Q3, Q4, Q5, Q6, Q7]), "radius" : 3 * mm, "tangentPropagation" : true, "allowEdgeOverflow" : false});
        }
    });
